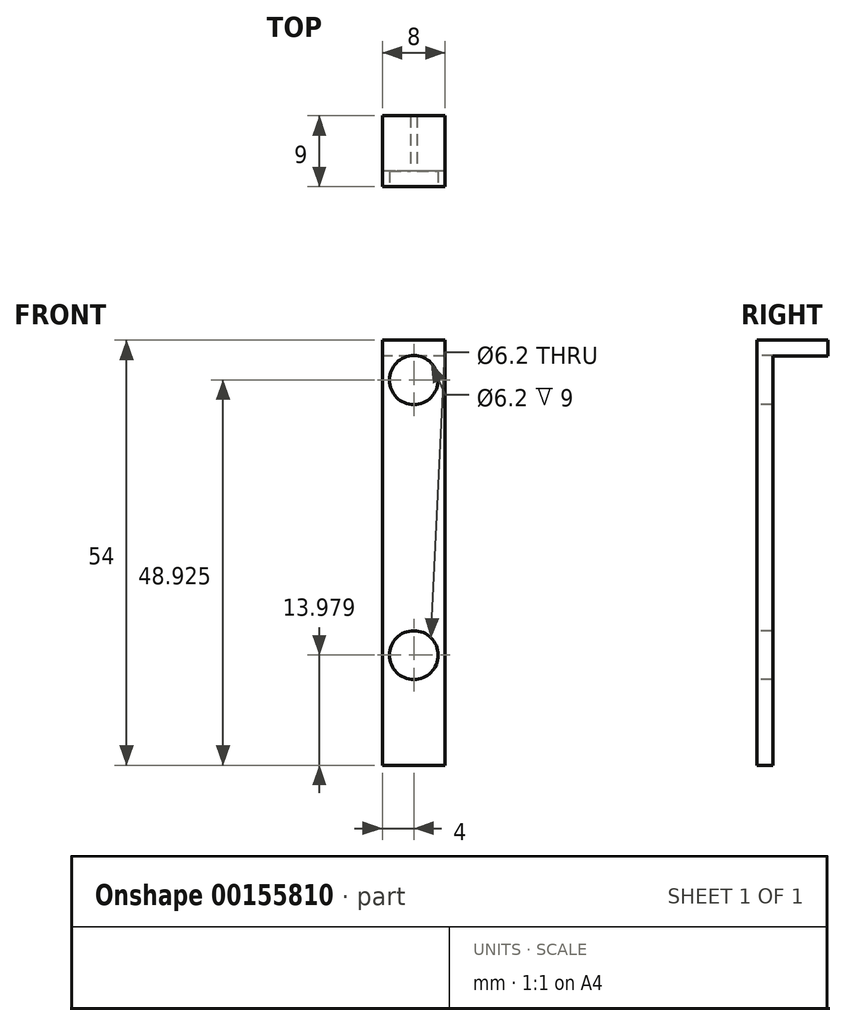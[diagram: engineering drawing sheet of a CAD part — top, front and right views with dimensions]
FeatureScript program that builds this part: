
annotation { "Feature Type Name" : "Feature", "Feature Type Description" : "" }
export const myFeature = defineFeature(function(context is Context, id is Id, definition is map)
    precondition{}
    {
        {
            var Q0;
            Q0=qCreatedBy(makeId("Right.planeOp"),FACE);
            var sketch = newSketch(context, id + "F0", { "sketchPlane" : qUnion([Q0])});
            skLineSegment(sketch, "E0", {"start": v(0, 0) * mm, "end": v(0, -52) * mm});
            skLineSegment(sketch, "E1", {"start": v(0, -52) * mm, "end": v(-2, -52) * mm});
            skLineSegment(sketch, "E2", {"start": v(-2, -52) * mm, "end": v(-2, 2) * mm});
            skLineSegment(sketch, "E3", {"start": v(-2, 2) * mm, "end": v(7, 2) * mm});
            skLineSegment(sketch, "E4", {"start": v(7, 2) * mm, "end": v(7, 0) * mm});
            skLineSegment(sketch, "E5", {"start": v(7, 0) * mm, "end": v(0, 0) * mm});
            skSolve(sketch);
        }
        {
            var Q0;
            Q0 = qSketchRegion(id + "F0", true);
            extrude(context, id + "F1", {"entities" : qUnion([Q0]), "depth" : 8 * mm});
        }
        {
            var Q0;
            Q0=makeQuery(id+"F1.opExtrude","SWEPT_FACE",FACE,{"disambiguationData":[OSD([sQuery(id+"F0.wireOp",EDGE,"E2")])]});
            var sketch = newSketch(context, id + "F2", { "sketchPlane" : qUnion([Q0])});
            skCircle(sketch, "E6", {"center": v(4, -3.07) * mm, "radius": 3.1 * mm});
            skPoint(sketch, "E6.centerSnap0", {"position": v(4, 2) * mm});
            skCircle(sketch, "E7", {"center": v(4, -38.02) * mm, "radius": 3.1 * mm});
            skPoint(sketch, "E7.centerSnap0", {"position": v(4, -52) * mm});
            skSolve(sketch);
        }
        {
            var Q0;
            Q0 = qSketchRegion(id + "F2", true);
            extrude(context, id + "F3", {"entities" : qUnion([Q0]), "operationType" : NewBodyOperationType.REMOVE, "oppositeDirection" : true, "depth" : 25 * mm});
        }
    });
